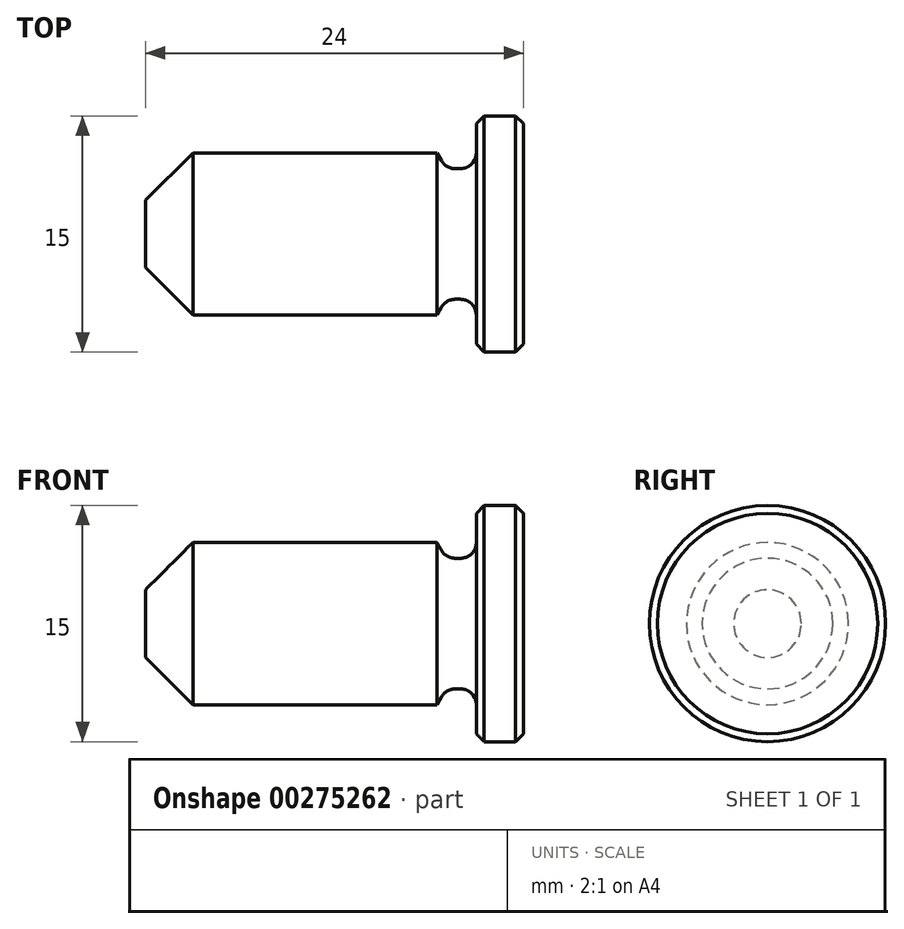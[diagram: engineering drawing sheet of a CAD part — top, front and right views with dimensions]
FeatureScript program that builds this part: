
annotation { "Feature Type Name" : "Feature", "Feature Type Description" : "" }
export const myFeature = defineFeature(function(context is Context, id is Id, definition is map)
    precondition{}
    {
        {
            var Q0;
            Q0=qCreatedBy(makeId("Front.planeOp"),FACE);
            var sketch = newSketch(context, id + "F0", { "sketchPlane" : qUnion([Q0])});
            skLineSegment(sketch, "E0", {"start": v(-12.64, 0) * mm, "end": v(11.36, 0) * mm});
            skLineSegment(sketch, "E1", {"start": v(11.36, 0) * mm, "end": v(11.36, 7.5) * mm});
            skLineSegment(sketch, "E2", {"start": v(11.36, 7.5) * mm, "end": v(8.36, 7.5) * mm});
            skLineSegment(sketch, "E3", {"start": v(-12.64, 0) * mm, "end": v(-12.64, 5.15) * mm});
            skLineSegment(sketch, "E4", {"start": v(-12.64, 5.15) * mm, "end": v(5.86, 5.15) * mm});
            skLineSegment(sketch, "E5", {"start": v(8.36, 7.5) * mm, "end": v(8.36, 5.15) * mm});
            skLineSegment(sketch, "E6", {"start": v(5.86, 5.15) * mm, "end": v(6.15, 4.65) * mm});
            skLineSegment(sketch, "E7", {"start": v(7.02, 4.15) * mm, "end": v(7.36, 4.15) * mm});
            skArc(sketch, "E8", {"start": v(6.15, 4.65) * mm, "mid": v(6.52, 4.28) * mm, "end": v(7.02, 4.15) * mm});
            skArc(sketch, "E9", {"start": v(7.36, 4.15) * mm, "mid": v(8.07, 4.44) * mm, "end": v(8.36, 5.15) * mm});
            skPoint(sketch, "E10", {"position": v(8.36, 5.15) * mm});
            skSolve(sketch);
        }
        {
            var Q0;
            Q0=makeQuery(id+"F0.imprint","IMPRINT",FACE,{"disambiguationData":[TD([[makeQuery(id+"F0.imprint","IMPRINT",EDGE,{"derivedFrom":sQuery(id+"F0.wireOp",EDGE,"E0")}),1.0]])]});
            var Q1;
            Q1=sQuery(id+"F0.wireOp",EDGE,"E0");
            revolve(context, id + "F1", {"entities" : qUnion([Q0]), "axis" : qUnion([Q1]), "revolveType" : RevolveType.FULL});
        }
        {
            var Q0;
            Q0=makeQuery(id+"F1.opRevolve","SWEPT_EDGE",EDGE,{"disambiguationData":[OSD([sQuery(id+"F0.wireOp",EDGE,"E1"),sQuery(id+"F0.wireOp",EDGE,"E2")])]});
            var Q1;
            Q1=makeQuery(id+"F1.opRevolve","SWEPT_EDGE",EDGE,{"disambiguationData":[OSD([sQuery(id+"F0.wireOp",EDGE,"E2"),sQuery(id+"F0.wireOp",EDGE,"E5")])]});
            chamfer(context, id + "F2", {"entities" : qUnion([Q0, Q1]), "width" : .5 * mm, "tangentPropagation" : true});
        }
        {
            var Q0;
            Q0=makeQuery(id+"F1.opRevolve","SWEPT_EDGE",EDGE,{"disambiguationData":[OSD([sQuery(id+"F0.wireOp",EDGE,"E3"),sQuery(id+"F0.wireOp",EDGE,"E4")])]});
            chamfer(context, id + "F3", {"entities" : qUnion([Q0]), "width" : 3 * mm, "tangentPropagation" : true});
        }
    });
